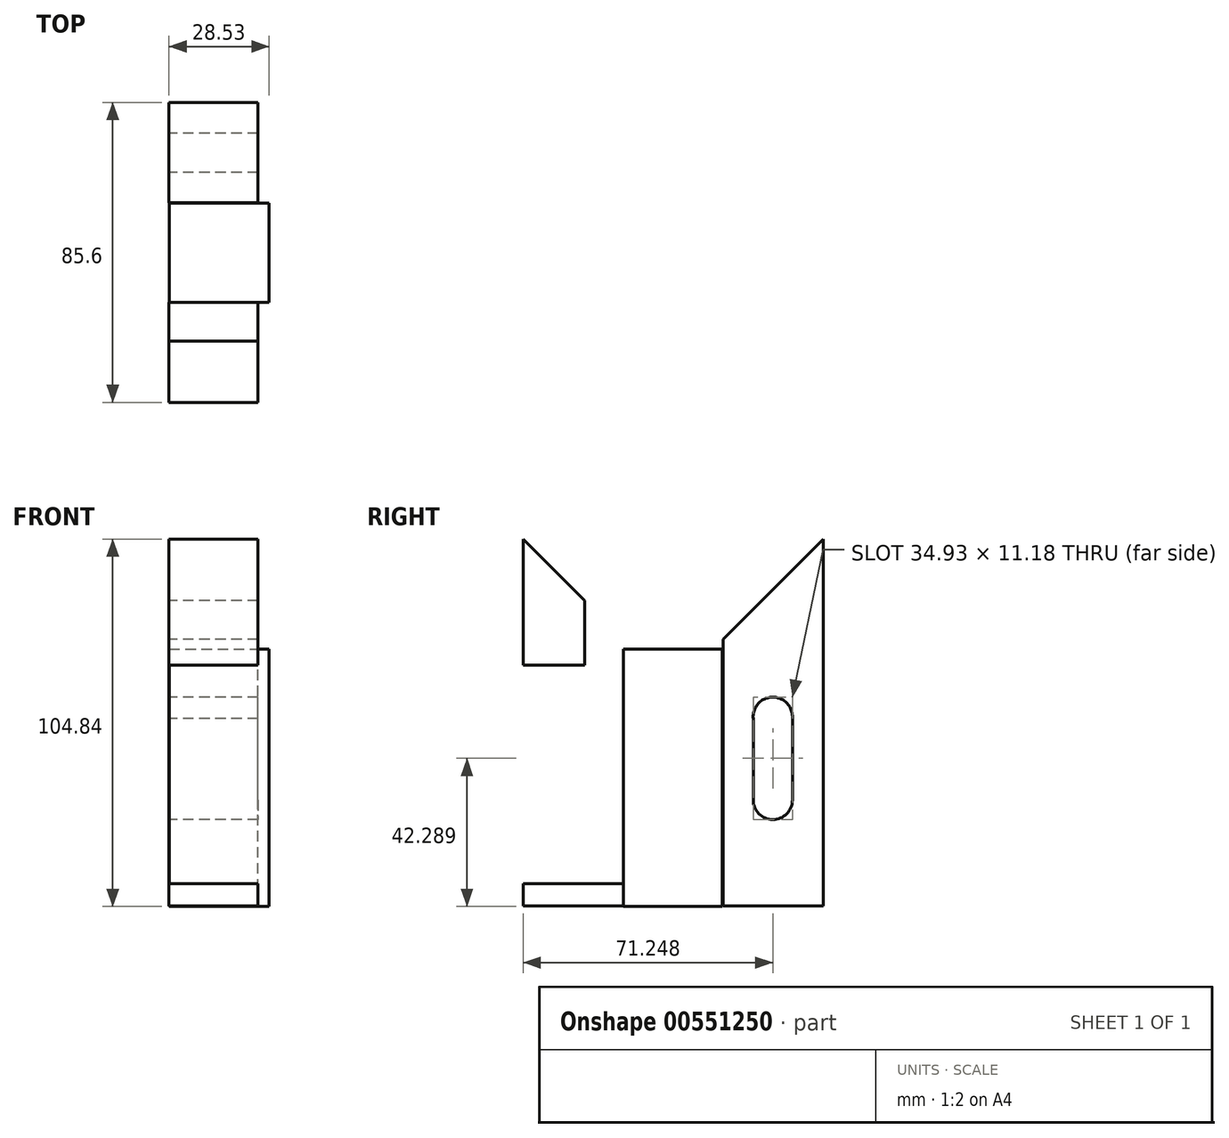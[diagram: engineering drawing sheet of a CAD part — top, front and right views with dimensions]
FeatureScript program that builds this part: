
annotation { "Feature Type Name" : "Feature", "Feature Type Description" : "" }
export const myFeature = defineFeature(function(context is Context, id is Id, definition is map)
    precondition{}
    {
        {
            var Q0;
            Q0=qCreatedBy(makeId("Top.planeOp"),FACE);
            var sketch = newSketch(context, id + "F0", { "sketchPlane" : qUnion([Q0])});
            skLineSegment(sketch, "E0.bottom", {"start": v(0.08, 14.02) * mm, "end": v(28.53, 14.02) * mm});
            skLineSegment(sketch, "E0.top", {"start": v(0.08, -14.22) * mm, "end": v(28.53, -14.22) * mm});
            skLineSegment(sketch, "E0.left", {"start": v(0.08, 14.02) * mm, "end": v(0.08, -14.22) * mm});
            skLineSegment(sketch, "E0.right", {"start": v(28.53, 14.02) * mm, "end": v(28.53, -14.22) * mm});
            skSolve(sketch);
        }
        {
            var Q0;
            Q0 = qSketchRegion(id + "F0", true);
            extrude(context, id + "F1", {"entities" : qUnion([Q0]), "endBound" : BoundingType.SYMMETRIC, "depth" : 73.4 * mm, "offsetDistance" : 25.4 * mm});
        }
        {
            var Q0;
            Q0=qCreatedBy(makeId("Right.planeOp"),FACE);
            var sketch = newSketch(context, id + "F2", { "sketchPlane" : qUnion([Q0])});
            skLineSegment(sketch, "E1", {"start": v(-14.22, -36.51) * mm, "end": v(-42.8, -36.51) * mm});
            skLineSegment(sketch, "E2", {"start": v(-42.8, -36.51) * mm, "end": v(-42.8, 68.14) * mm});
            skLineSegment(sketch, "E3", {"start": v(-14.22, -36.51) * mm, "end": v(-14.22, 39.56) * mm});
            skLineSegment(sketch, "E4", {"start": v(-42.8, 68.14) * mm, "end": v(-14.22, 39.56) * mm});
            skLineSegment(sketch, "E5", {"start": v(-42.8, 32.12) * mm, "end": v(-25.27, 32.12) * mm});
            skLineSegment(sketch, "E6", {"start": v(-25.27, 32.12) * mm, "end": v(-25.27, 50.6) * mm});
            skArc(sketch, "E7", {"start": v(-34.04, -6.29) * mm, "mid": v(-28.45, -11.87) * mm, "end": v(-22.86, -6.29) * mm});
            skLineSegment(sketch, "E8", {"start": v(-34.04, -8.58) * mm, "end": v(-34.04, 16.97) * mm});
            skArc(sketch, "E9", {"start": v(-22.86, 16.97) * mm, "mid": v(-28.45, 23.05) * mm, "end": v(-34.04, 16.97) * mm});
            skLineSegment(sketch, "E10.MirrorCS", {"start": v(-42.8, -30.16) * mm, "end": v(-14.22, -30.16) * mm});
            skLineSegment(sketch, "E11.MirrorCS", {"start": v(-22.86, -8.11) * mm, "end": v(-22.86, 17.44) * mm});
            skLineSegment(sketch, "E12.MirrorCS", {"start": v(42.8, -36.51) * mm, "end": v(42.8, 68.14) * mm});
            skArc(sketch, "E13.MirrorCS", {"start": v(22.86, 16.97) * mm, "mid": v(28.45, 23.05) * mm, "end": v(34.04, 16.97) * mm});
            skLineSegment(sketch, "E14.MirrorCS", {"start": v(34.04, -8.58) * mm, "end": v(34.04, 16.97) * mm});
            skLineSegment(sketch, "E15.MirrorCS", {"start": v(42.8, 32.12) * mm, "end": v(25.27, 32.12) * mm});
            skLineSegment(sketch, "E16.MirrorCS", {"start": v(25.27, 32.12) * mm, "end": v(25.27, 50.6) * mm});
            skLineSegment(sketch, "E17.MirrorCS", {"start": v(22.86, -8.11) * mm, "end": v(22.86, 17.44) * mm});
            skLineSegment(sketch, "E18.MirrorCS", {"start": v(42.8, 68.14) * mm, "end": v(14.22, 39.56) * mm});
            skArc(sketch, "E19.MirrorCS", {"start": v(34.04, -6.29) * mm, "mid": v(28.45, -11.87) * mm, "end": v(22.86, -6.29) * mm});
            skLineSegment(sketch, "E20.MirrorCS", {"start": v(14.22, -36.51) * mm, "end": v(42.8, -36.51) * mm});
            skLineSegment(sketch, "E21.MirrorCS", {"start": v(42.8, -30.16) * mm, "end": v(14.22, -30.16) * mm});
            skLineSegment(sketch, "E22.MirrorCS", {"start": v(14.22, -36.51) * mm, "end": v(14.22, 39.56) * mm});
            skSolve(sketch);
        }
        {
            var Q0;
            {var subQ6=sQuery(id+"F2.wireOp",EDGE,"E9");Q0=makeQuery(id+"F2.imprint","IMPRINT",FACE,{"disambiguationData":[TD([[makeQuery(id+"F2.imprint","IMPRINT",EDGE,{"derivedFrom":subQ6}),-1.0]])]});}
            var Q1;
            {var subQ4=sQuery(id+"F2.wireOp",EDGE,"E5");Q1=makeQuery(id+"F2.imprint","IMPRINT",FACE,{"disambiguationData":[TD([[makeQuery(id+"F2.imprint","IMPRINT",EDGE,{"derivedFrom":subQ4}),1.0]])]});}
            var Q2;
            {var subQ2=sQuery(id+"F2.wireOp",EDGE,"E10.MirrorCS");Q2=makeQuery(id+"F2.imprint","IMPRINT",FACE,{"disambiguationData":[TD([[makeQuery(id+"F2.imprint","IMPRINT",EDGE,{"derivedFrom":subQ2}),-1.0]])]});}
            var Q3;
            {var subQ7=sQuery(id+"F2.wireOp",EDGE,"E21.MirrorCS");Q3=makeQuery(id+"F2.imprint","IMPRINT",FACE,{"disambiguationData":[TD([[makeQuery(id+"F2.imprint","IMPRINT",EDGE,{"derivedFrom":subQ7}),-1.0]])]});}
            var Q4;
            {var subQ0=sQuery(id+"F2.wireOp",EDGE,"E20.MirrorCS");Q4=makeQuery(id+"F2.imprint","IMPRINT",FACE,{"disambiguationData":[TD([[makeQuery(id+"F2.imprint","IMPRINT",EDGE,{"derivedFrom":subQ0}),1.0]])]});}
            var Q5;
            {var subQ4=sQuery(id+"F2.wireOp",EDGE,"E15.MirrorCS");Q5=makeQuery(id+"F2.imprint","IMPRINT",FACE,{"disambiguationData":[TD([[makeQuery(id+"F2.imprint","IMPRINT",EDGE,{"derivedFrom":subQ4}),-1.0]])]});}
            extrude(context, id + "F3", {"entities" : qUnion([Q0, Q1, Q2, Q3, Q4, Q5]), "operationType" : NewBodyOperationType.ADD, "depth" : 25.4 * mm, "offsetDistance" : 25.4 * mm});
        }
    });
